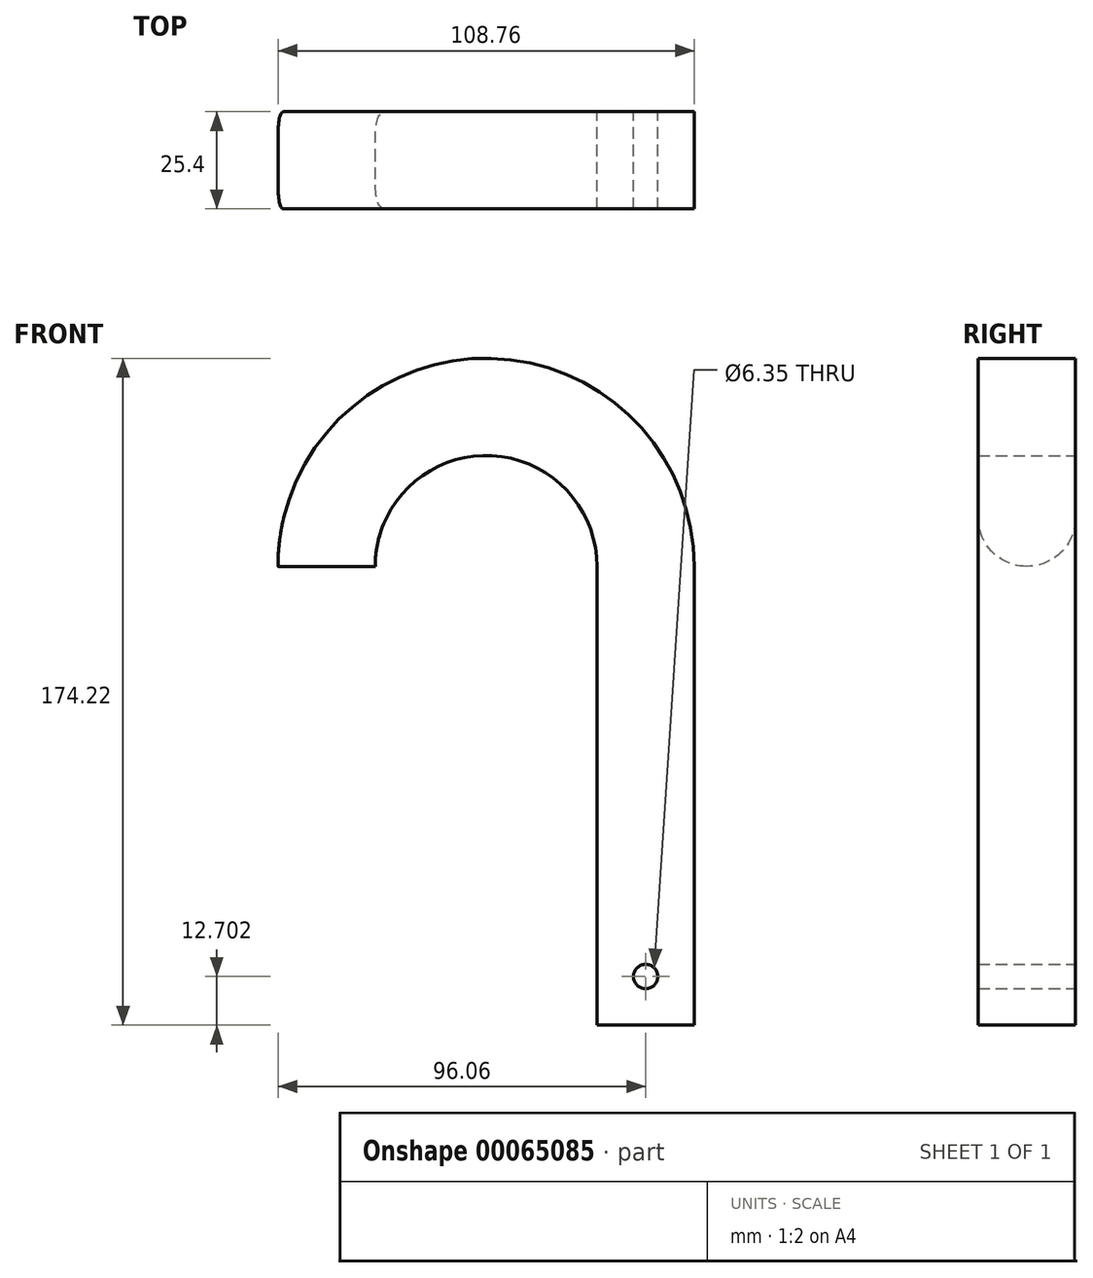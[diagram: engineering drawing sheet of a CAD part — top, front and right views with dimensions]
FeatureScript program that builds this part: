
annotation { "Feature Type Name" : "Feature", "Feature Type Description" : "" }
export const myFeature = defineFeature(function(context is Context, id is Id, definition is map)
    precondition{}
    {
        {
            var Q0;
            Q0=qCreatedBy(makeId("Front.planeOp"),FACE);
            var sketch = newSketch(context, id + "F0", { "sketchPlane" : qUnion([Q0])});
            skLineSegment(sketch, "E0.top", {"start": v(0, -74.95) * mm, "end": v(25.4, -74.95) * mm});
            skLineSegment(sketch, "E0.left", {"start": v(0, 44.9) * mm, "end": v(0, -74.95) * mm});
            skLineSegment(sketch, "E0.right", {"start": v(25.4, 44.9) * mm, "end": v(25.4, -74.95) * mm});
            skArc(sketch, "E1", {"start": v(0, 44.9) * mm, "mid": v(-28.98, 73.87) * mm, "end": v(-57.95, 44.9) * mm});
            skLineSegment(sketch, "E2", {"start": v(-57.95, 44.9) * mm, "end": v(-83.35, 44.9) * mm});
            skArc(sketch, "E3", {"start": v(-83.35, 44.9) * mm, "mid": v(-28.98, 99.27) * mm, "end": v(25.4, 44.9) * mm});
            skCircle(sketch, "E4", {"center": v(12.7, -62.25) * mm, "radius": 3.18 * mm});
            skSolve(sketch);
        }
        {
            var Q0;
            Q0 = qSketchRegion(id + "F0", true);
            extrude(context, id + "F1", {"entities" : qUnion([Q0]), "depth" : 25.4 * mm});
        }
        {
            var Q0;
            Q0=makeQuery(id+"F1.opExtrude","CAP_EDGE",EDGE,{"disambiguationData":[OSD([sQuery(id+"F0.wireOp",EDGE,"E2")])],"isStart":false});
            fillet(context, id + "F2", {"entities" : qUnion([Q0]), "radius" : 12.7 * mm, "tangentPropagation" : true, "allowEdgeOverflow" : false});
        }
        {
            var Q0;
            Q0=makeQuery(id+"F1.opExtrude","CAP_EDGE",EDGE,{"disambiguationData":[OSD([sQuery(id+"F0.wireOp",EDGE,"E2")])],"isStart":true});
            fillet(context, id + "F3", {"entities" : qUnion([Q0]), "radius" : 12.7 * mm, "tangentPropagation" : true, "allowEdgeOverflow" : false});
        }
    });
